# Revit family: AF250 series
name_source: partatom
category: Modelos genéricos
revit_build: Autodesk Revit 2017 (Build: 20181011_1645(x64)
units: mm (PartAtom-declared; Revit-internal decimal feet)

## family parameters
Compartido = No
Corte con vacíos al cargar = No
Cota de conector redondo = Diámetro de uso
Puede alojar armadura = No
Punto de cálculo de habitación = No
Se basa en plano de trabajo = No
Siempre vertical = Sí
Tipo de pieza = Normal

## types (3) — shared parameters
Anchura exterior = 316 mm  [stored 1.03675 ft]
Anchura interior = 250 mm  [stored 0.82021 ft]
Clase de carga = F-900 Norma EN-1433
Descripción = Arqueta de Hormigón Polímero tipo ULMA para recogida de aguas pluviales.
Fabricante = ULMA Architectural
Ficha técnica = http://www.ulmaarchitectural.com
Longitud = 500 mm  [stored 1.64042 ft]
Peso = 0.00 kg
Serie canales = F250K + S300F
URL = http://www.ulmaarchitectural.com
Ø salida frontal = 0 mm

## per-type parameters (varying)
| type | Altura | Costo | Diseño | Ø salida lateral |
| AF250S + A250B | 750 mm  [stored 2.46063 ft] | 187.09 $ | 2 cuerpos | 200 mm |
| AF250-65 + A250B415 | 916 mm | 308.46 $ | 2 cuerpos | 415 mm |
| AF250-65 + A250I + A250B415 | 1316 mm  [stored 4.31759 ft] | 389.4 $ | 3 cuerpos | 415 mm |

note: column(s) folded — value = type name in every type: Modelo

note: [stored X ft] marks values corroborated as IEEE doubles in the binary element streams (Revit-internal decimal feet)
